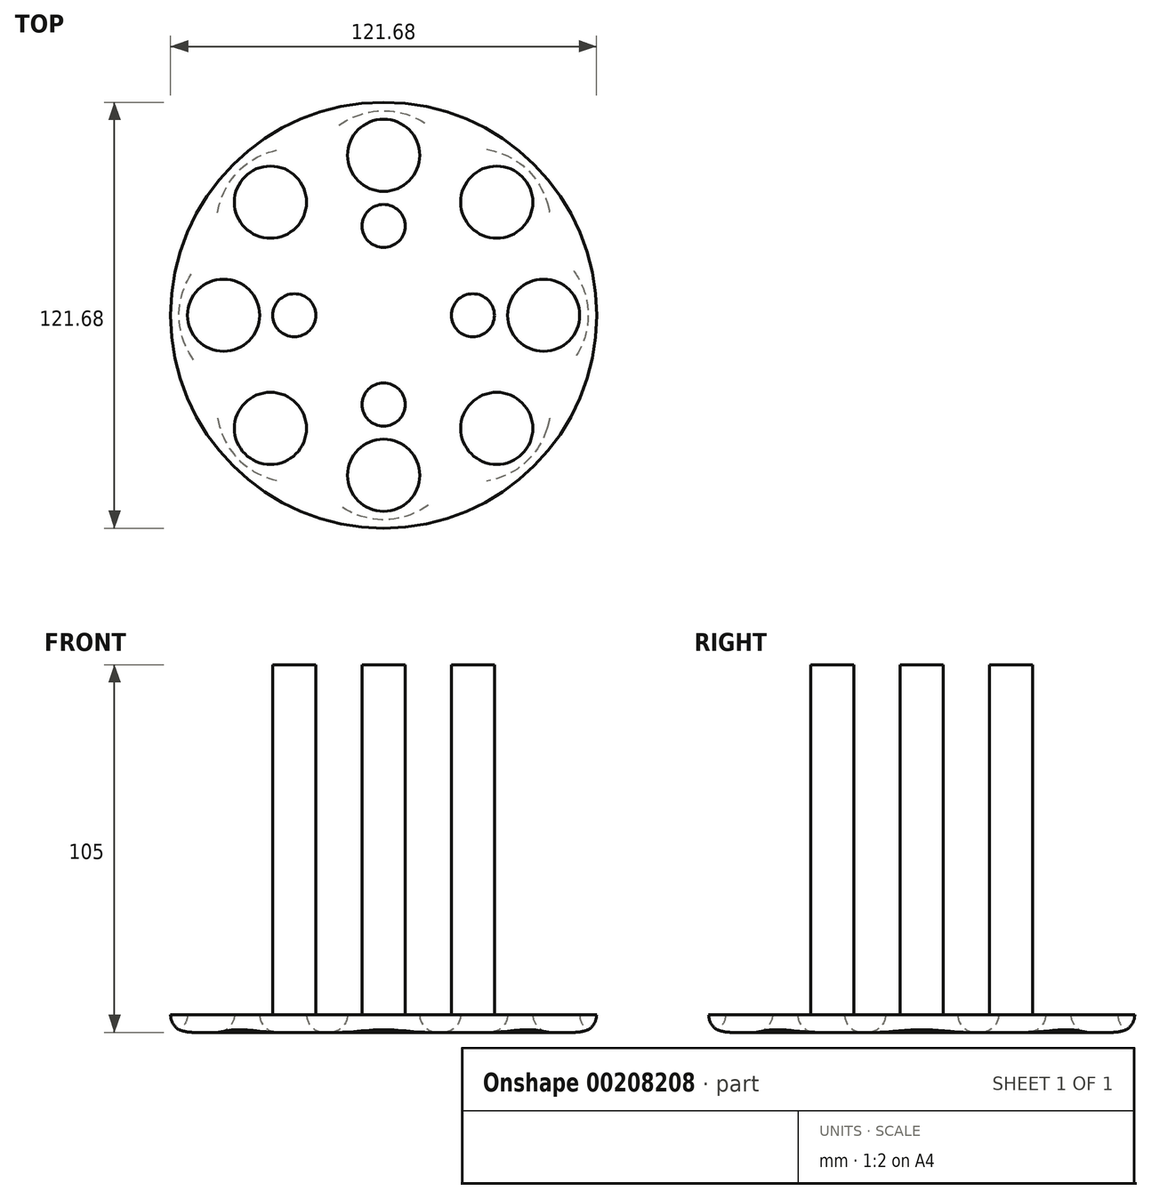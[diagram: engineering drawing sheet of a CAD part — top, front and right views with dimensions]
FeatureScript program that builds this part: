
annotation { "Feature Type Name" : "Feature", "Feature Type Description" : "" }
export const myFeature = defineFeature(function(context is Context, id is Id, definition is map)
    precondition{}
    {
        {
            var Q0;
            Q0=qCreatedBy(makeId("Top.planeOp"),FACE);
            var sketch = newSketch(context, id + "F0", { "sketchPlane" : qUnion([Q0])});
            skCircle(sketch, "E0", {"center": v(0, 0) * mm, "radius": 60.84 * mm});
            skCircle(sketch, "E1", {"center": v(0, 45.7) * mm, "radius": 10.3 * mm});
            skCircle(sketch, "E2.1.0", {"center": v(-32.32, 32.32) * mm, "radius": 10.3 * mm});
            skCircle(sketch, "E2.2.0", {"center": v(-45.7, 0) * mm, "radius": 10.3 * mm});
            skCircle(sketch, "E2.3.0", {"center": v(-32.32, -32.32) * mm, "radius": 10.3 * mm});
            skCircle(sketch, "E2.4.0", {"center": v(0, -45.7) * mm, "radius": 10.3 * mm});
            skCircle(sketch, "E2.5.0", {"center": v(32.32, -32.32) * mm, "radius": 10.3 * mm});
            skCircle(sketch, "E2.6.0", {"center": v(45.7, 0) * mm, "radius": 10.3 * mm});
            skCircle(sketch, "E2.7.0", {"center": v(32.32, 32.32) * mm, "radius": 10.3 * mm});
            skSolve(sketch);
        }
        {
            var Q0;
            Q0=makeQuery(id+"F0.imprint","IMPRINT",FACE,{"disambiguationData":[TD([[makeQuery(id+"F0.imprint","IMPRINT",EDGE,{"derivedFrom":sQuery(id+"F0.wireOp",EDGE,"E0")}),1.0]])]});
            extrude(context, id + "F1", {"entities" : qUnion([Q0]), "depth" : 5 * mm});
        }
        {
            var Q0;
            Q0=makeQuery(id+"F1.opExtrude","CAP_FACE",FACE,{"disambiguationData":[OSD([sQuery(id+"F0.wireOp",EDGE,"E0"),sQuery(id+"F0.wireOp",EDGE,"E1"),sQuery(id+"F0.wireOp",EDGE,"E2.1.0"),sQuery(id+"F0.wireOp",EDGE,"E2.2.0"),sQuery(id+"F0.wireOp",EDGE,"E2.3.0"),sQuery(id+"F0.wireOp",EDGE,"E2.4.0"),sQuery(id+"F0.wireOp",EDGE,"E2.5.0"),sQuery(id+"F0.wireOp",EDGE,"E2.6.0"),sQuery(id+"F0.wireOp",EDGE,"E2.7.0")])],"isStart":true});
            fillet(context, id + "F2", {"entities" : qUnion([Q0]), "radius" : 5.08 * mm, "tangentPropagation" : true, "allowEdgeOverflow" : false});
        }
        {
            var Q0;
            Q0=makeQuery(id+"F1.opExtrude","CAP_FACE",FACE,{"disambiguationData":[OSD([sQuery(id+"F0.wireOp",EDGE,"E0"),sQuery(id+"F0.wireOp",EDGE,"E1"),sQuery(id+"F0.wireOp",EDGE,"E2.1.0"),sQuery(id+"F0.wireOp",EDGE,"E2.2.0"),sQuery(id+"F0.wireOp",EDGE,"E2.3.0"),sQuery(id+"F0.wireOp",EDGE,"E2.4.0"),sQuery(id+"F0.wireOp",EDGE,"E2.5.0"),sQuery(id+"F0.wireOp",EDGE,"E2.6.0"),sQuery(id+"F0.wireOp",EDGE,"E2.7.0")])],"isStart":false});
            var sketch = newSketch(context, id + "F3", { "sketchPlane" : qUnion([Q0])});
            skCircle(sketch, "E3", {"center": v(0, 25.5) * mm, "radius": 6.15 * mm});
            skCircle(sketch, "E4.1.0", {"center": v(-25.5, 0) * mm, "radius": 6.15 * mm});
            skCircle(sketch, "E4.2.0", {"center": v(0, -25.5) * mm, "radius": 6.15 * mm});
            skCircle(sketch, "E4.3.0", {"center": v(25.5, 0) * mm, "radius": 6.15 * mm});
            skPoint(sketch, "E4.center", {"position": v(0, 0) * mm});
            skSolve(sketch);
        }
        {
            var Q0;
            Q0 = qSketchRegion(id + "F3", true);
            extrude(context, id + "F4", {"entities" : qUnion([Q0]), "operationType" : NewBodyOperationType.ADD, "depth" : 100 * mm});
        }
    });
